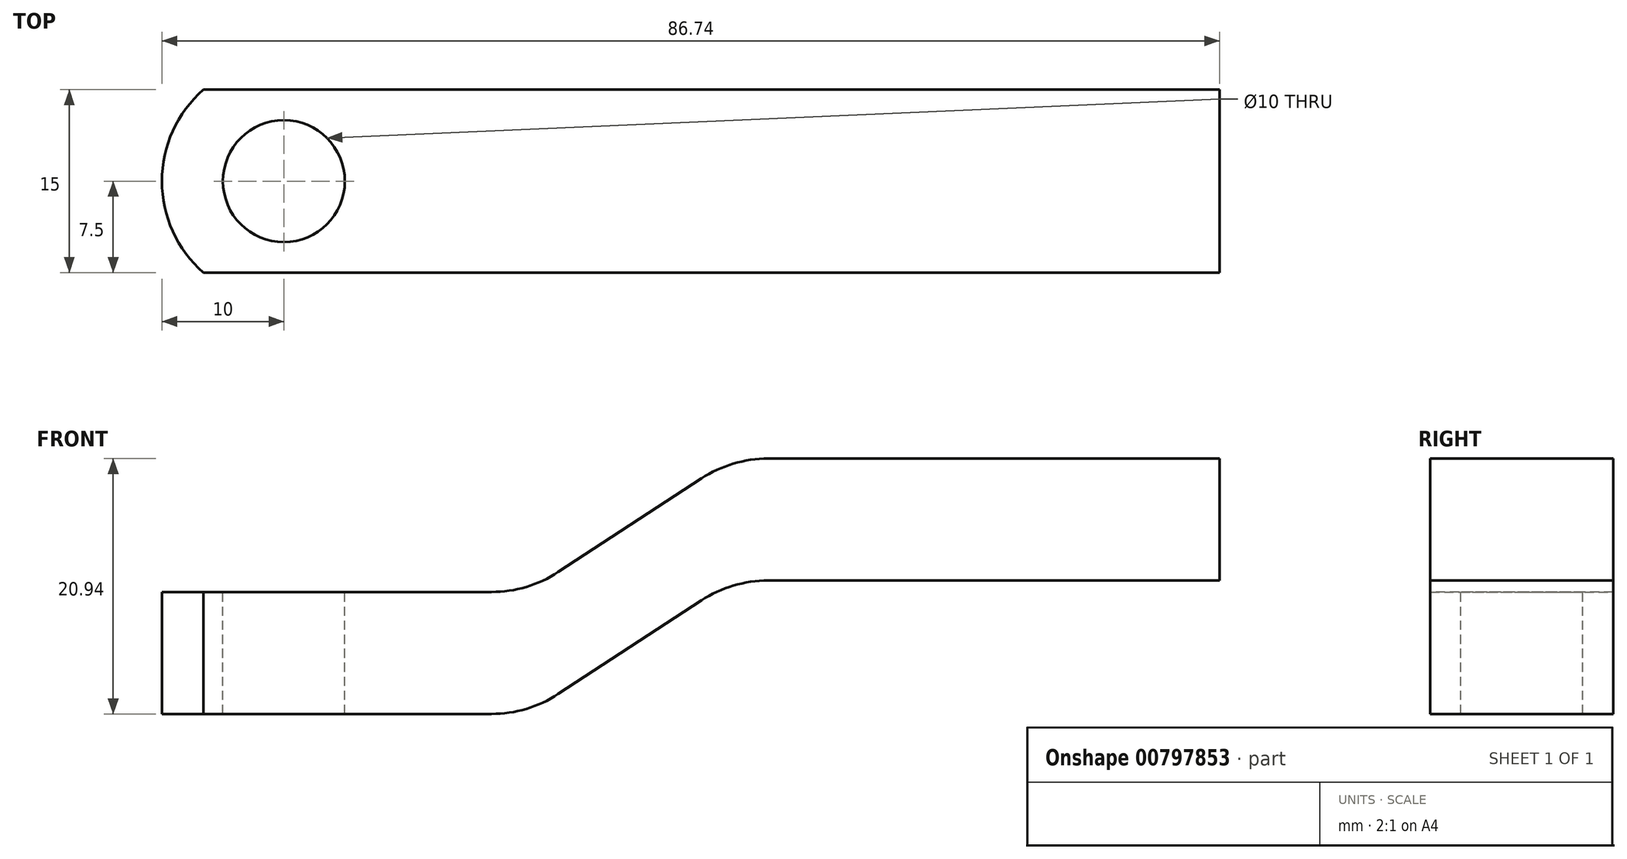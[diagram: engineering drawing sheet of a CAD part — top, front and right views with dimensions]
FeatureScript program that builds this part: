
annotation { "Feature Type Name" : "Feature", "Feature Type Description" : "" }
export const myFeature = defineFeature(function(context is Context, id is Id, definition is map)
    precondition{}
    {
        {
            var Q0;
            Q0=qCreatedBy(makeId("Front.planeOp"),FACE);
            var sketch = newSketch(context, id + "F0", { "sketchPlane" : qUnion([Q0])});
            skLineSegment(sketch, "E0", {"start": v(0, 0) * mm, "end": v(0, 10) * mm});
            skLineSegment(sketch, "E1", {"start": v(0, 10) * mm, "end": v(27.02, 10) * mm});
            skLineSegment(sketch, "E2", {"start": v(0, 0) * mm, "end": v(27.02, 0) * mm});
            skLineSegment(sketch, "E3", {"start": v(32.5, 11.63) * mm, "end": v(44.25, 19.3) * mm});
            skLineSegment(sketch, "E4", {"start": v(32.5, 1.63) * mm, "end": v(44.25, 9.3) * mm});
            skLineSegment(sketch, "E5", {"start": v(49.72, 10.94) * mm, "end": v(86.74, 10.94) * mm});
            skLineSegment(sketch, "E6", {"start": v(49.72, 20.94) * mm, "end": v(86.74, 20.94) * mm});
            skLineSegment(sketch, "E7", {"start": v(86.74, 20.94) * mm, "end": v(86.74, 10.94) * mm});
            skPoint(sketch, "E8.visualSharp", {"position": v(30, 10) * mm});
            skArc(sketch, "E8.filletArc", {"start": v(27.02, 10) * mm, "mid": v(29.88, 10.42) * mm, "end": v(32.5, 11.63) * mm});
            skPoint(sketch, "E9.visualSharp", {"position": v(30, 0) * mm});
            skArc(sketch, "E9.filletArc", {"start": v(27.02, 0) * mm, "mid": v(29.88, 0.42) * mm, "end": v(32.5, 1.63) * mm});
            skPoint(sketch, "E10.visualSharp", {"position": v(46.74, 20.94) * mm});
            skArc(sketch, "E10.filletArc", {"start": v(49.72, 20.94) * mm, "mid": v(46.87, 20.52) * mm, "end": v(44.25, 19.3) * mm});
            skPoint(sketch, "E11.visualSharp", {"position": v(46.74, 10.94) * mm});
            skArc(sketch, "E11.filletArc", {"start": v(49.72, 10.94) * mm, "mid": v(46.87, 10.52) * mm, "end": v(44.25, 9.3) * mm});
            skSolve(sketch);
        }
        {
            var Q0;
            Q0 = qSketchRegion(id + "F0", true);
            extrude(context, id + "F1", {"entities" : qUnion([Q0]), "endBound" : BoundingType.SYMMETRIC, "depth" : 15 * mm, "offsetDistance" : 25 * mm});
        }
        {
            var Q0;
            Q0=makeQuery(id+"F1.opExtrude","SWEPT_FACE",FACE,{"disambiguationData":[OSD([sQuery(id+"F0.wireOp",EDGE,"E1")])]});
            var sketch = newSketch(context, id + "F2", { "sketchPlane" : qUnion([Q0])});
            skCircle(sketch, "E12", {"center": v(10, 0) * mm, "radius": 5 * mm});
            skSolve(sketch);
        }
        {
            var Q0;
            Q0 = qSketchRegion(id + "F2", true);
            extrude(context, id + "F3", {"entities" : qUnion([Q0]), "operationType" : NewBodyOperationType.REMOVE, "endBound" : BoundingType.THROUGH_ALL, "oppositeDirection" : true, "depth" : 25 * mm, "offsetDistance" : 25 * mm});
        }
        {
            var Q0;
            Q0=makeQuery(id+"F1.opExtrude","SWEPT_FACE",FACE,{"disambiguationData":[OSD([sQuery(id+"F0.wireOp",EDGE,"E1")])]});
            var sketch = newSketch(context, id + "F4", { "sketchPlane" : qUnion([Q0])});
            skArc(sketch, "E13", {"start": v(3.39, 7.5) * mm, "mid": v(0, 0) * mm, "end": v(3.39, -7.5) * mm});
            skLineSegment(sketch, "E14", {"start": v(3.39, 7.5) * mm, "end": v(0, 7.5) * mm});
            skLineSegment(sketch, "E15", {"start": v(0, 7.5) * mm, "end": v(0, 0) * mm});
            skLineSegment(sketch, "E16", {"start": v(0, 0) * mm, "end": v(0, -7.5) * mm});
            skLineSegment(sketch, "E17", {"start": v(0, -7.5) * mm, "end": v(3.39, -7.5) * mm});
            skSolve(sketch);
        }
        {
            var Q0;
            Q0 = qSketchRegion(id + "F4", true);
            extrude(context, id + "F5", {"entities" : qUnion([Q0]), "operationType" : NewBodyOperationType.REMOVE, "endBound" : BoundingType.THROUGH_ALL, "oppositeDirection" : true, "depth" : 25 * mm, "offsetDistance" : 25 * mm});
        }
    });
